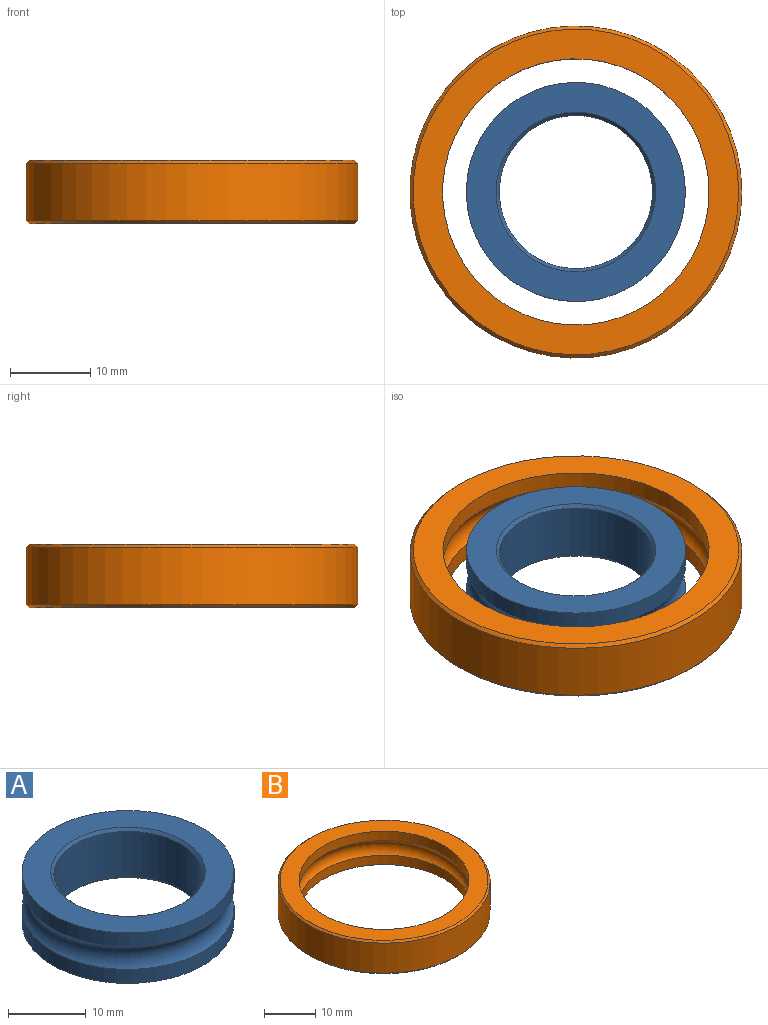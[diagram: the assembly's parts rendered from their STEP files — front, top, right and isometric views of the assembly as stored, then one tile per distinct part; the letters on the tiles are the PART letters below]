
ASSEMBLY  parts=2 mates=2
PART A: 8 faces, bbox 32.6x32.6x7.9 mm
  f0: torus R=15.08mm, axis (0,0,1), area 330.6mm2, adj f4,f5
  f1: cone r=9.92mm half-angle=45deg, axis (0,0,1), area 34.3mm2, adj f2,f6
  f2: cylinder r=9.53mm len=19.05mm, axis (0,0,1), area 427.5mm2, adj f1,f3
  f3: cone r=9.53mm half-angle=45deg, axis (0,0,-1), area 34.3mm2, adj f2,f7
  f4: cylinder r=13.62mm len=27.23mm, axis (0,0,1), area 188.6mm2, adj f0,f7
  f5: cylinder r=13.62mm len=27.23mm, axis (0,0,1), area 188.6mm2, adj f0,f6
  f6: plane 27.23x27.23mm, normal (0,0,1), area 273.2mm2, adj f1,f5
  f7: plane 27.23x27.23mm, normal (0,0,-1), area 273.2mm2, adj f3,f4
PART B: 8 faces, bbox 41.3x41.3x7.9 mm
  f0: cylinder r=16.55mm len=33.09mm, axis (0,0,1), area 229.2mm2, adj f1,f7
  f1: torus R=15.08mm, axis (0,0,1), area 432.2mm2, adj f0,f2
  f2: cylinder r=16.55mm len=33.09mm, axis (0,0,1), area 229.2mm2, adj f1,f6
  f3: cone r=20.24mm half-angle=45deg, axis (0,0,1), area 72.1mm2, adj f4,f6
  f4: cylinder r=20.64mm len=41.28mm, axis (0,0,1), area 926.3mm2, adj f3,f5
  f5: cone r=20.64mm half-angle=45deg, axis (0,0,-1), area 72.1mm2, adj f4,f7
  f6: plane 40.48x40.48mm, normal (0,0,-1), area 426.9mm2, adj f2,f3
  f7: plane 40.48x40.48mm, normal (0,0,1), area 426.9mm2, adj f0,f5
PLACE A t=(-12.47,-5.65,2.32)mm
PLACE B t=(-12.47,-5.65,2.32)mm
MATE planar A.f0 <-> B.f0  axis (0,0,1) through (-12.47,-5.65,6.29)mm
MATE cylindrical A.f0 <-> B.f0  axis (0,0,1) through (-12.47,-5.65,2.32)mm
